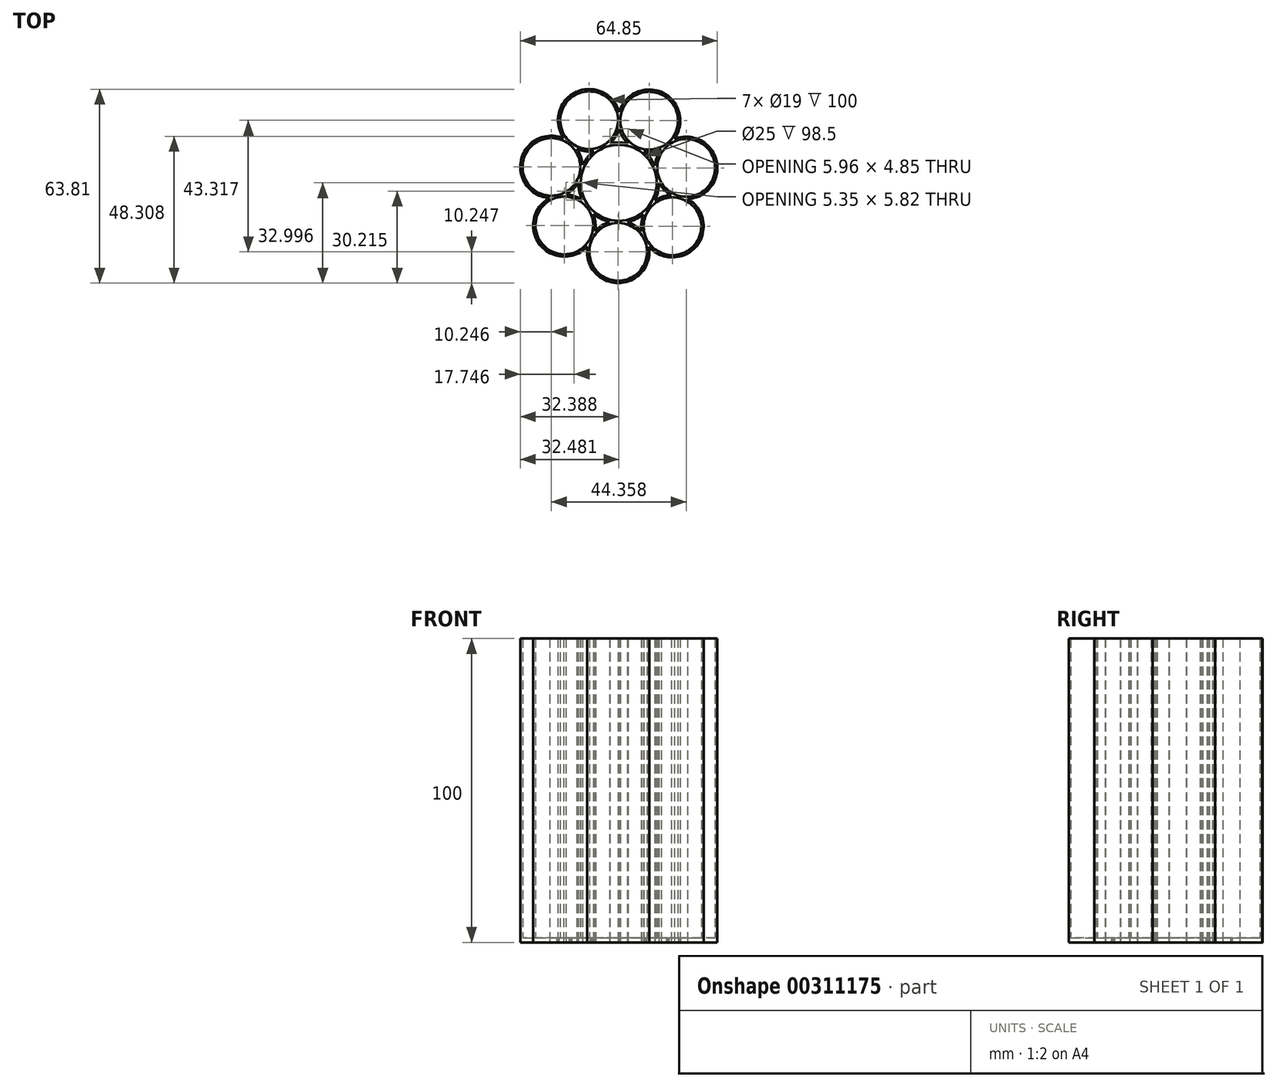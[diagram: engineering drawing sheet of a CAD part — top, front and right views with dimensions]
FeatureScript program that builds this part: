
annotation { "Feature Type Name" : "Feature", "Feature Type Description" : "" }
export const myFeature = defineFeature(function(context is Context, id is Id, definition is map)
    precondition{}
    {
        {
            var Q0;
            Q0=qCreatedBy(makeId("Top.planeOp"),FACE);
            var sketch = newSketch(context, id + "F0", { "sketchPlane" : qUnion([Q0])});
            skCircle(sketch, "E0", {"center": v(39.41, 7.56) * mm, "radius": 9.5 * mm});
            skCircle(sketch, "E1", {"center": v(39.58, 30.3) * mm, "radius": 12.5 * mm});
            skCircle(sketch, "E2", {"center": v(39.58, 30.3) * mm, "radius": 13.25 * mm});
            skCircle(sketch, "E3", {"center": v(39.41, 7.56) * mm, "radius": 10.25 * mm});
            skCircle(sketch, "E4.1.0", {"center": v(57.26, 16) * mm, "radius": 10.25 * mm});
            skCircle(sketch, "E4.2.0", {"center": v(61.8, 35.2) * mm, "radius": 10.25 * mm});
            skCircle(sketch, "E4.3.0", {"center": v(49.6, 50.73) * mm, "radius": 10.25 * mm});
            skCircle(sketch, "E4.4.0", {"center": v(29.86, 50.87) * mm, "radius": 10.25 * mm});
            skCircle(sketch, "E4.5.0", {"center": v(17.44, 35.53) * mm, "radius": 10.25 * mm});
            skCircle(sketch, "E4.6.0", {"center": v(21.69, 16.25) * mm, "radius": 10.25 * mm});
            skCircle(sketch, "E5", {"center": v(61.8, 35.2) * mm, "radius": 9.5 * mm});
            skCircle(sketch, "E6", {"center": v(49.6, 50.73) * mm, "radius": 9.5 * mm});
            skCircle(sketch, "E7", {"center": v(29.86, 50.87) * mm, "radius": 9.5 * mm});
            skCircle(sketch, "E8", {"center": v(17.44, 35.53) * mm, "radius": 9.5 * mm});
            skCircle(sketch, "E9", {"center": v(21.69, 16.25) * mm, "radius": 9.5 * mm});
            skCircle(sketch, "E10", {"center": v(57.26, 16) * mm, "radius": 9.5 * mm});
            skSolve(sketch);
        }
        {
            var Q0;
            Q0 = qSketchRegion(id + "F0", true);
            var Q1;
            {var subQ0=sQuery(id+"F0.wireOp",EDGE,"E4.5.0");var subQ1=sQuery(id+"F0.wireOp",EDGE,"E2");var subQ2=makeQuery(id+"F0.imprint","INTERSECT",VERTEX,{"disambiguationData":[OD(0.0)],"derivedFrom":[subQ1,subQ0]});Q1=makeQuery(id+"F0.imprint","IMPRINT",FACE,{"disambiguationData":[TD([[makeQuery(id+"F0.imprint","IMPRINT",EDGE,{"disambiguationData":[TD([[subQ2,-1.0]])],"derivedFrom":subQ1}),-1.0]])]});}
            var Q2;
            {var subQ0=sQuery(id+"F0.wireOp",EDGE,"E7");var subQ1=sQuery(id+"F0.wireOp",EDGE,"E2");var subQ2=makeQuery(id+"F0.imprint","INTERSECT",VERTEX,{"derivedFrom":[subQ1,subQ0]});Q2=makeQuery(id+"F0.imprint","IMPRINT",FACE,{"disambiguationData":[TD([[makeQuery(id+"F0.imprint","IMPRINT",EDGE,{"disambiguationData":[TD([[subQ2,-1.0]])],"derivedFrom":subQ1}),-1.0]])]});}
            var Q3;
            {var subQ0=sQuery(id+"F0.wireOp",EDGE,"E4.4.0");var subQ1=sQuery(id+"F0.wireOp",EDGE,"E1");var subQ2=makeQuery(id+"F0.imprint","INTERSECT",VERTEX,{"derivedFrom":[subQ1,subQ0]});Q3=makeQuery(id+"F0.imprint","IMPRINT",FACE,{"disambiguationData":[TD([[makeQuery(id+"F0.imprint","IMPRINT",EDGE,{"disambiguationData":[TD([[subQ2,-1.0]])],"derivedFrom":subQ1}),-1.0]])]});}
            var Q4;
            {var subQ0=sQuery(id+"F0.wireOp",EDGE,"E4.4.0");var subQ1=sQuery(id+"F0.wireOp",EDGE,"E2");var subQ2=makeQuery(id+"F0.imprint","INTERSECT",VERTEX,{"disambiguationData":[OD(0.0)],"derivedFrom":[subQ1,subQ0]});Q4=makeQuery(id+"F0.imprint","IMPRINT",FACE,{"disambiguationData":[TD([[makeQuery(id+"F0.imprint","IMPRINT",EDGE,{"disambiguationData":[TD([[subQ2,-1.0]])],"derivedFrom":subQ1}),1.0]])]});}
            var Q5;
            {var subQ0=sQuery(id+"F0.wireOp",EDGE,"E4.4.0");var subQ1=sQuery(id+"F0.wireOp",EDGE,"E2");var subQ2=makeQuery(id+"F0.imprint","INTERSECT",VERTEX,{"disambiguationData":[OD(0.0)],"derivedFrom":[subQ1,subQ0]});Q5=makeQuery(id+"F0.imprint","IMPRINT",FACE,{"disambiguationData":[TD([[makeQuery(id+"F0.imprint","IMPRINT",EDGE,{"disambiguationData":[TD([[subQ2,-1.0]])],"derivedFrom":subQ1}),-1.0]])]});}
            var Q6;
            {var subQ0=sQuery(id+"F0.wireOp",EDGE,"E4.3.0");var subQ1=sQuery(id+"F0.wireOp",EDGE,"E1");var subQ2=makeQuery(id+"F0.imprint","INTERSECT",VERTEX,{"derivedFrom":[subQ1,subQ0]});Q6=makeQuery(id+"F0.imprint","IMPRINT",FACE,{"disambiguationData":[TD([[makeQuery(id+"F0.imprint","IMPRINT",EDGE,{"disambiguationData":[TD([[subQ2,-1.0]])],"derivedFrom":subQ1}),-1.0]])]});}
            var Q7;
            {var subQ0=sQuery(id+"F0.wireOp",EDGE,"E4.3.0");var subQ1=sQuery(id+"F0.wireOp",EDGE,"E2");var subQ2=makeQuery(id+"F0.imprint","INTERSECT",VERTEX,{"disambiguationData":[OD(0.0)],"derivedFrom":[subQ1,subQ0]});Q7=makeQuery(id+"F0.imprint","IMPRINT",FACE,{"disambiguationData":[TD([[makeQuery(id+"F0.imprint","IMPRINT",EDGE,{"disambiguationData":[TD([[subQ2,-1.0]])],"derivedFrom":subQ1}),1.0]])]});}
            var Q8;
            {var subQ0=sQuery(id+"F0.wireOp",EDGE,"E4.3.0");var subQ1=sQuery(id+"F0.wireOp",EDGE,"E1");var subQ2=makeQuery(id+"F0.imprint","INTERSECT",VERTEX,{"derivedFrom":[subQ1,subQ0]});Q8=makeQuery(id+"F0.imprint","IMPRINT",FACE,{"disambiguationData":[TD([[makeQuery(id+"F0.imprint","IMPRINT",EDGE,{"disambiguationData":[TD([[subQ2,1.0]])],"derivedFrom":subQ1}),-1.0]])]});}
            var Q9;
            {var subQ0=sQuery(id+"F0.wireOp",EDGE,"E6");var subQ1=sQuery(id+"F0.wireOp",EDGE,"E2");var subQ2=makeQuery(id+"F0.imprint","INTERSECT",VERTEX,{"derivedFrom":[subQ1,subQ0]});Q9=makeQuery(id+"F0.imprint","IMPRINT",FACE,{"disambiguationData":[TD([[makeQuery(id+"F0.imprint","IMPRINT",EDGE,{"disambiguationData":[TD([[subQ2,-1.0]])],"derivedFrom":subQ1}),-1.0]])]});}
            var Q10;
            {var subQ0=sQuery(id+"F0.wireOp",EDGE,"E4.2.0");var subQ1=sQuery(id+"F0.wireOp",EDGE,"E2");var subQ2=makeQuery(id+"F0.imprint","INTERSECT",VERTEX,{"disambiguationData":[OD(0.0)],"derivedFrom":[subQ1,subQ0]});Q10=makeQuery(id+"F0.imprint","IMPRINT",FACE,{"disambiguationData":[TD([[makeQuery(id+"F0.imprint","IMPRINT",EDGE,{"disambiguationData":[TD([[subQ2,1.0]])],"derivedFrom":subQ1}),1.0]])]});}
            var Q11;
            {var subQ0=sQuery(id+"F0.wireOp",EDGE,"E5");var subQ1=sQuery(id+"F0.wireOp",EDGE,"E2");var subQ2=makeQuery(id+"F0.imprint","INTERSECT",VERTEX,{"derivedFrom":[subQ1,subQ0]});Q11=makeQuery(id+"F0.imprint","IMPRINT",FACE,{"disambiguationData":[TD([[makeQuery(id+"F0.imprint","IMPRINT",EDGE,{"disambiguationData":[TD([[subQ2,1.0]])],"derivedFrom":subQ1}),-1.0]])]});}
            var Q12;
            {var subQ0=sQuery(id+"F0.wireOp",EDGE,"E4.2.0");var subQ1=sQuery(id+"F0.wireOp",EDGE,"E2");var subQ2=makeQuery(id+"F0.imprint","INTERSECT",VERTEX,{"disambiguationData":[OD(0.0)],"derivedFrom":[subQ1,subQ0]});Q12=makeQuery(id+"F0.imprint","IMPRINT",FACE,{"disambiguationData":[TD([[makeQuery(id+"F0.imprint","IMPRINT",EDGE,{"disambiguationData":[TD([[subQ2,1.0]])],"derivedFrom":subQ1}),-1.0]])]});}
            var Q13;
            {var subQ0=sQuery(id+"F0.wireOp",EDGE,"E4.3.0");var subQ1=sQuery(id+"F0.wireOp",EDGE,"E2");var subQ2=makeQuery(id+"F0.imprint","INTERSECT",VERTEX,{"disambiguationData":[OD(0.0)],"derivedFrom":[subQ1,subQ0]});Q13=makeQuery(id+"F0.imprint","IMPRINT",FACE,{"disambiguationData":[TD([[makeQuery(id+"F0.imprint","IMPRINT",EDGE,{"disambiguationData":[TD([[subQ2,-1.0]])],"derivedFrom":subQ1}),-1.0]])]});}
            var Q14;
            {var subQ0=sQuery(id+"F0.wireOp",EDGE,"E4.2.0");var subQ1=sQuery(id+"F0.wireOp",EDGE,"E1");var subQ2=makeQuery(id+"F0.imprint","INTERSECT",VERTEX,{"derivedFrom":[subQ1,subQ0]});Q14=makeQuery(id+"F0.imprint","IMPRINT",FACE,{"disambiguationData":[TD([[makeQuery(id+"F0.imprint","IMPRINT",EDGE,{"disambiguationData":[TD([[subQ2,1.0]])],"derivedFrom":subQ1}),-1.0]])]});}
            var Q15;
            {var subQ0=sQuery(id+"F0.wireOp",EDGE,"E10");var subQ1=sQuery(id+"F0.wireOp",EDGE,"E2");var subQ2=makeQuery(id+"F0.imprint","INTERSECT",VERTEX,{"derivedFrom":[subQ1,subQ0]});Q15=makeQuery(id+"F0.imprint","IMPRINT",FACE,{"disambiguationData":[TD([[makeQuery(id+"F0.imprint","IMPRINT",EDGE,{"disambiguationData":[TD([[subQ2,-1.0]])],"derivedFrom":subQ1}),-1.0]])]});}
            var Q16;
            {var subQ0=sQuery(id+"F0.wireOp",EDGE,"E4.1.0");var subQ1=sQuery(id+"F0.wireOp",EDGE,"E2");var subQ2=makeQuery(id+"F0.imprint","INTERSECT",VERTEX,{"disambiguationData":[OD(0.0)],"derivedFrom":[subQ1,subQ0]});Q16=makeQuery(id+"F0.imprint","IMPRINT",FACE,{"disambiguationData":[TD([[makeQuery(id+"F0.imprint","IMPRINT",EDGE,{"disambiguationData":[TD([[subQ2,-1.0]])],"derivedFrom":subQ1}),-1.0]])]});}
            var Q17;
            {var subQ0=sQuery(id+"F0.wireOp",EDGE,"E3");var subQ1=sQuery(id+"F0.wireOp",EDGE,"E1");var subQ2=makeQuery(id+"F0.imprint","INTERSECT",VERTEX,{"derivedFrom":[subQ1,subQ0]});Q17=makeQuery(id+"F0.imprint","IMPRINT",FACE,{"disambiguationData":[TD([[makeQuery(id+"F0.imprint","IMPRINT",EDGE,{"disambiguationData":[TD([[subQ2,-1.0]])],"derivedFrom":subQ1}),-1.0]])]});}
            var Q18;
            {var subQ0=sQuery(id+"F0.wireOp",EDGE,"E4.1.0");var subQ1=sQuery(id+"F0.wireOp",EDGE,"E2");var subQ2=makeQuery(id+"F0.imprint","INTERSECT",VERTEX,{"disambiguationData":[OD(0.0)],"derivedFrom":[subQ1,subQ0]});Q18=makeQuery(id+"F0.imprint","IMPRINT",FACE,{"disambiguationData":[TD([[makeQuery(id+"F0.imprint","IMPRINT",EDGE,{"disambiguationData":[TD([[subQ2,-1.0]])],"derivedFrom":subQ1}),1.0]])]});}
            var Q19;
            {var subQ0=sQuery(id+"F0.wireOp",EDGE,"E2");var subQ1=makeQuery(id+"F0.imprint","INTERSECT",VERTEX,{"derivedFrom":[sQuery(id+"F0.wireOp",EDGE,"E0"),subQ0]});Q19=makeQuery(id+"F0.imprint","IMPRINT",FACE,{"disambiguationData":[TD([[makeQuery(id+"F0.imprint","IMPRINT",EDGE,{"disambiguationData":[TD([[subQ1,1.0]])],"derivedFrom":subQ0}),1.0]])]});}
            var Q20;
            {var subQ0=sQuery(id+"F0.wireOp",EDGE,"E4.1.0");var subQ1=sQuery(id+"F0.wireOp",EDGE,"E0");var subQ2=makeQuery(id+"F0.imprint","INTERSECT",VERTEX,{"disambiguationData":[OD(0.0)],"derivedFrom":[subQ1,subQ0]});Q20=makeQuery(id+"F0.imprint","IMPRINT",FACE,{"disambiguationData":[TD([[makeQuery(id+"F0.imprint","IMPRINT",EDGE,{"disambiguationData":[TD([[subQ2,-1.0]])],"derivedFrom":subQ1}),-1.0]])]});}
            var Q21;
            {var subQ0=sQuery(id+"F0.wireOp",EDGE,"E2");var subQ1=sQuery(id+"F0.wireOp",EDGE,"E0");var subQ2=makeQuery(id+"F0.imprint","INTERSECT",VERTEX,{"derivedFrom":[subQ1,subQ0]});Q21=makeQuery(id+"F0.imprint","IMPRINT",FACE,{"disambiguationData":[TD([[makeQuery(id+"F0.imprint","IMPRINT",EDGE,{"disambiguationData":[TD([[subQ2,-1.0]])],"derivedFrom":subQ1}),-1.0]])]});}
            var Q22;
            {var subQ0=sQuery(id+"F0.wireOp",EDGE,"E4.6.0");var subQ1=sQuery(id+"F0.wireOp",EDGE,"E1");var subQ2=makeQuery(id+"F0.imprint","INTERSECT",VERTEX,{"derivedFrom":[subQ1,subQ0]});Q22=makeQuery(id+"F0.imprint","IMPRINT",FACE,{"disambiguationData":[TD([[makeQuery(id+"F0.imprint","IMPRINT",EDGE,{"disambiguationData":[TD([[subQ2,-1.0]])],"derivedFrom":subQ1}),-1.0]])]});}
            var Q23;
            {var subQ0=sQuery(id+"F0.wireOp",EDGE,"E9");var subQ1=sQuery(id+"F0.wireOp",EDGE,"E2");var subQ2=makeQuery(id+"F0.imprint","INTERSECT",VERTEX,{"derivedFrom":[subQ1,subQ0]});Q23=makeQuery(id+"F0.imprint","IMPRINT",FACE,{"disambiguationData":[TD([[makeQuery(id+"F0.imprint","IMPRINT",EDGE,{"disambiguationData":[TD([[subQ2,-1.0]])],"derivedFrom":subQ1}),-1.0]])]});}
            var Q24;
            {var subQ0=sQuery(id+"F0.wireOp",EDGE,"E4.6.0");var subQ1=sQuery(id+"F0.wireOp",EDGE,"E2");var subQ2=makeQuery(id+"F0.imprint","INTERSECT",VERTEX,{"disambiguationData":[OD(0.0)],"derivedFrom":[subQ1,subQ0]});Q24=makeQuery(id+"F0.imprint","IMPRINT",FACE,{"disambiguationData":[TD([[makeQuery(id+"F0.imprint","IMPRINT",EDGE,{"disambiguationData":[TD([[subQ2,-1.0]])],"derivedFrom":subQ1}),1.0]])]});}
            var Q25;
            {var subQ0=sQuery(id+"F0.wireOp",EDGE,"E4.6.0");var subQ1=sQuery(id+"F0.wireOp",EDGE,"E2");var subQ2=makeQuery(id+"F0.imprint","INTERSECT",VERTEX,{"disambiguationData":[OD(0.0)],"derivedFrom":[subQ1,subQ0]});Q25=makeQuery(id+"F0.imprint","IMPRINT",FACE,{"disambiguationData":[TD([[makeQuery(id+"F0.imprint","IMPRINT",EDGE,{"disambiguationData":[TD([[subQ2,-1.0]])],"derivedFrom":subQ1}),-1.0]])]});}
            var Q26;
            {var subQ0=sQuery(id+"F0.wireOp",EDGE,"E4.5.0");var subQ1=sQuery(id+"F0.wireOp",EDGE,"E1");var subQ2=makeQuery(id+"F0.imprint","INTERSECT",VERTEX,{"derivedFrom":[subQ1,subQ0]});Q26=makeQuery(id+"F0.imprint","IMPRINT",FACE,{"disambiguationData":[TD([[makeQuery(id+"F0.imprint","IMPRINT",EDGE,{"disambiguationData":[TD([[subQ2,-1.0]])],"derivedFrom":subQ1}),-1.0]])]});}
            var Q27;
            {var subQ0=sQuery(id+"F0.wireOp",EDGE,"E4.5.0");var subQ1=sQuery(id+"F0.wireOp",EDGE,"E2");var subQ2=makeQuery(id+"F0.imprint","INTERSECT",VERTEX,{"disambiguationData":[OD(0.0)],"derivedFrom":[subQ1,subQ0]});Q27=makeQuery(id+"F0.imprint","IMPRINT",FACE,{"disambiguationData":[TD([[makeQuery(id+"F0.imprint","IMPRINT",EDGE,{"disambiguationData":[TD([[subQ2,-1.0]])],"derivedFrom":subQ1}),1.0]])]});}
            var Q28;
            {var subQ0=sQuery(id+"F0.wireOp",EDGE,"E8");var subQ1=sQuery(id+"F0.wireOp",EDGE,"E2");var subQ2=makeQuery(id+"F0.imprint","INTERSECT",VERTEX,{"derivedFrom":[subQ1,subQ0]});Q28=makeQuery(id+"F0.imprint","IMPRINT",FACE,{"disambiguationData":[TD([[makeQuery(id+"F0.imprint","IMPRINT",EDGE,{"disambiguationData":[TD([[subQ2,-1.0]])],"derivedFrom":subQ1}),-1.0]])]});}
            extrude(context, id + "F1", {"entities" : qUnion([Q0, Q1, Q2, Q3, Q4, Q5, Q6, Q7, Q8, Q9, Q10, Q11, Q12, Q13, Q14, Q15, Q16, Q17, Q18, Q19, Q20, Q21, Q22, Q23, Q24, Q25, Q26, Q27, Q28]), "depth" : 100 * mm});
        }
        {
            var Q0;
            {var subQ0=sQuery(id+"F0.wireOp",EDGE,"E8");var subQ1=sQuery(id+"F0.wireOp",EDGE,"E4.4.0");var subQ2=makeQuery(id+"F0.imprint","INTERSECT",VERTEX,{"disambiguationData":[OD(0.0)],"derivedFrom":[subQ1,subQ0]});Q0=makeQuery(id+"F0.imprint","IMPRINT",FACE,{"disambiguationData":[TD([[makeQuery(id+"F0.imprint","IMPRINT",EDGE,{"disambiguationData":[TD([[subQ2,-1.0]])],"derivedFrom":subQ1}),-1.0]])]});}
            var Q1;
            {var subQ0=sQuery(id+"F0.wireOp",EDGE,"E9");var subQ1=sQuery(id+"F0.wireOp",EDGE,"E3");var subQ7=makeQuery(id+"F0.imprint","INTERSECT",VERTEX,{"disambiguationData":[OD(0.0)],"derivedFrom":[subQ1,subQ0]});Q1=makeQuery(id+"F0.imprint","IMPRINT",FACE,{"disambiguationData":[TD([[makeQuery(id+"F0.imprint","IMPRINT",EDGE,{"disambiguationData":[TD([[subQ7,-1.0]])],"derivedFrom":subQ1}),-1.0]])]});}
            var Q2;
            {var subQ0=sQuery(id+"F0.wireOp",EDGE,"E4.1.0");var subQ1=sQuery(id+"F0.wireOp",EDGE,"E0");var subQ5=makeQuery(id+"F0.imprint","INTERSECT",VERTEX,{"disambiguationData":[OD(0.0)],"derivedFrom":[subQ1,subQ0]});Q2=makeQuery(id+"F0.imprint","IMPRINT",FACE,{"disambiguationData":[TD([[makeQuery(id+"F0.imprint","IMPRINT",EDGE,{"disambiguationData":[TD([[subQ5,-1.0]])],"derivedFrom":subQ1}),1.0]])]});}
            var Q3;
            {var subQ0=sQuery(id+"F0.wireOp",EDGE,"E1");var subQ4=makeQuery(id+"F0.imprint","INTERSECT",VERTEX,{"derivedFrom":[subQ0,sQuery(id+"F0.wireOp",EDGE,"E4.3.0")]});Q3=makeQuery(id+"F0.imprint","IMPRINT",FACE,{"disambiguationData":[TD([[makeQuery(id+"F0.imprint","IMPRINT",EDGE,{"disambiguationData":[TD([[subQ4,1.0]])],"derivedFrom":subQ0}),1.0]])]});}
            var Q4;
            {var subQ0=sQuery(id+"F0.wireOp",EDGE,"E10");var subQ2=sQuery(id+"F0.wireOp",EDGE,"E3");var subQ7=makeQuery(id+"F0.imprint","INTERSECT",VERTEX,{"disambiguationData":[OD(0.0)],"derivedFrom":[subQ2,subQ0]});Q4=makeQuery(id+"F0.imprint","IMPRINT",FACE,{"disambiguationData":[TD([[makeQuery(id+"F0.imprint","IMPRINT",EDGE,{"disambiguationData":[TD([[subQ7,-1.0]])],"derivedFrom":subQ2}),-1.0]])]});}
            var Q5;
            {var subQ0=sQuery(id+"F0.wireOp",EDGE,"E5");var subQ2=sQuery(id+"F0.wireOp",EDGE,"E4.1.0");var subQ6=makeQuery(id+"F0.imprint","INTERSECT",VERTEX,{"disambiguationData":[OD(0.0)],"derivedFrom":[subQ2,subQ0]});Q5=makeQuery(id+"F0.imprint","IMPRINT",FACE,{"disambiguationData":[TD([[makeQuery(id+"F0.imprint","IMPRINT",EDGE,{"disambiguationData":[TD([[subQ6,-1.0]])],"derivedFrom":subQ2}),-1.0]])]});}
            var Q6;
            {var subQ0=sQuery(id+"F0.wireOp",EDGE,"E6");var subQ2=sQuery(id+"F0.wireOp",EDGE,"E4.2.0");var subQ7=makeQuery(id+"F0.imprint","INTERSECT",VERTEX,{"disambiguationData":[OD(0.0)],"derivedFrom":[subQ2,subQ0]});Q6=makeQuery(id+"F0.imprint","IMPRINT",FACE,{"disambiguationData":[TD([[makeQuery(id+"F0.imprint","IMPRINT",EDGE,{"disambiguationData":[TD([[subQ7,-1.0]])],"derivedFrom":subQ2}),-1.0]])]});}
            var Q7;
            {var subQ0=sQuery(id+"F0.wireOp",EDGE,"E7");var subQ1=sQuery(id+"F0.wireOp",EDGE,"E4.3.0");var subQ2=makeQuery(id+"F0.imprint","INTERSECT",VERTEX,{"disambiguationData":[OD(0.0)],"derivedFrom":[subQ1,subQ0]});Q7=makeQuery(id+"F0.imprint","IMPRINT",FACE,{"disambiguationData":[TD([[makeQuery(id+"F0.imprint","IMPRINT",EDGE,{"disambiguationData":[TD([[subQ2,-1.0]])],"derivedFrom":subQ1}),-1.0]])]});}
            extrude(context, id + "F2", {"entities" : qUnion([Q0, Q1, Q2, Q3, Q4, Q5, Q6, Q7]), "operationType" : NewBodyOperationType.ADD, "depth" : 1.5 * mm});
        }
    });
